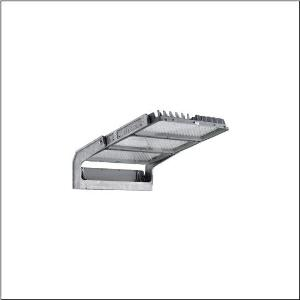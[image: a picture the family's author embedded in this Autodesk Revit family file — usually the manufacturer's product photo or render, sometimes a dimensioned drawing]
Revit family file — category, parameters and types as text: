
# Revit family: floodlight_fl_11_maxi_pro___rs08_5xa779224l01ab_f570
name_source: partatom
category: Lighting Fixtures
units: mm (PartAtom-declared; Revit-internal decimal feet)

## family parameters
Cut with Voids When Loaded = No
Host = Face
Light Source = No
Part Type = Normal
Room Calculation Point = No
Round Connector Dimension = Use Diameter
Shared = No

## types (1)
- --- (1 x LED, 152180 lm, 1633.1 W, 5700K)
    Apparent Load = 1633 VA
    CIE Flux Codes = 70 87 98 100 100
    Color Rendering = 90
    Color Temperature = 5700K
    Default Elevation = 1800 mm
    Description = Floodlight FL 11  maxi  pro floodlight; light control with lens of PMMA; cover panel of toughened safety glass, transparent; light distribution: RS08, rotationally symmetric direct distribution, LED; colour temperature: 5700K, rated luminous flux: 152.180lm, colour rendering: CRI > 90, light colour: 957; luminous efficacy: 93lm/W; brightness control: DMX+RDM; with terminal, 8-pole, max. 2.5mm², mains connection: 220..240V/380..400V AC, 50/60Hz, surge voltage resistance: line to ground: 10kV, LED service life up to 100,000h L90. Typical operating time: 1000h per year., ECG replaceable separately, LED unit replaceable without ESD environment, dustproof LED module, dimming range 10..100%; 1633W floodlight with 3x LED unit of diecast aluminium, coated grey; length: 1.003mm / width: 651mm / height: 338mm; mounting bracket, of diecast aluminium, uncoated, natural, equipment: Power, protection rating (complete): IP66; insulation class (complete): insulation class I (protective earthing); certification: CE, ENEC, VDE; ball protection: ball impact resistant, only for outdoor installations in the designated locations, permissible operating ambient temperature: -40..+55°C, permissible storage temperature: -40..+85°Cpackaging unit: 1 piece

Light Distribution: RS08
    Height = 320 mm
    Lamp = 1 x LED
    Lamp Light Flux = 152180 lm
    Lamp Power = 1633.1 W
    Lamp count = 1
    Length = 1002 mm
    Luminous efficacy = 93 lm/W
    Manufacturer = Siteco
    ModVariant = No
    Model = 5XA779224L01AB
    Mounting Place = Ceiling
    Mounting Type = Surface mounted
    Number of Poles = 1
    OnlyDefault = Yes
    Power Factor = 1
    Product Name = Floodlight FL 11 maxi pro | RS08
    Product group = floodlight | ceiling mounted
    ProductGroupID = 303
    Protection Class = Protection class I
    Protection Degree = IP 66
    RLX_Detail_Level = 1
    RLX_Emergency_Light_Flux = 0 lm
    RLX_Emergency_Type = 0
    RLX_Emergency_Type_DB = No
    RlxData = <blob elided: 40261 chars, md5=57d58896>
    Socket = socket
    Standby Power = 0 W
    System Light Flux = 152180 lm
    System Power = 1633 W
    Type Comments = factory setting: luminous flux: 100 % | dim-lin: 255 | 1100 mA
    Type Image = l_1356210.jpg
    URL = http://relux.com
    VarID = @adj_033803
    Voltage = 0 V
    Weight = 0.00 kg
    Width = 655 mm

## geometry (parser evidence)
native form markers: Blend x4, Sweep x12
no freeform markers — native parametric forms only
